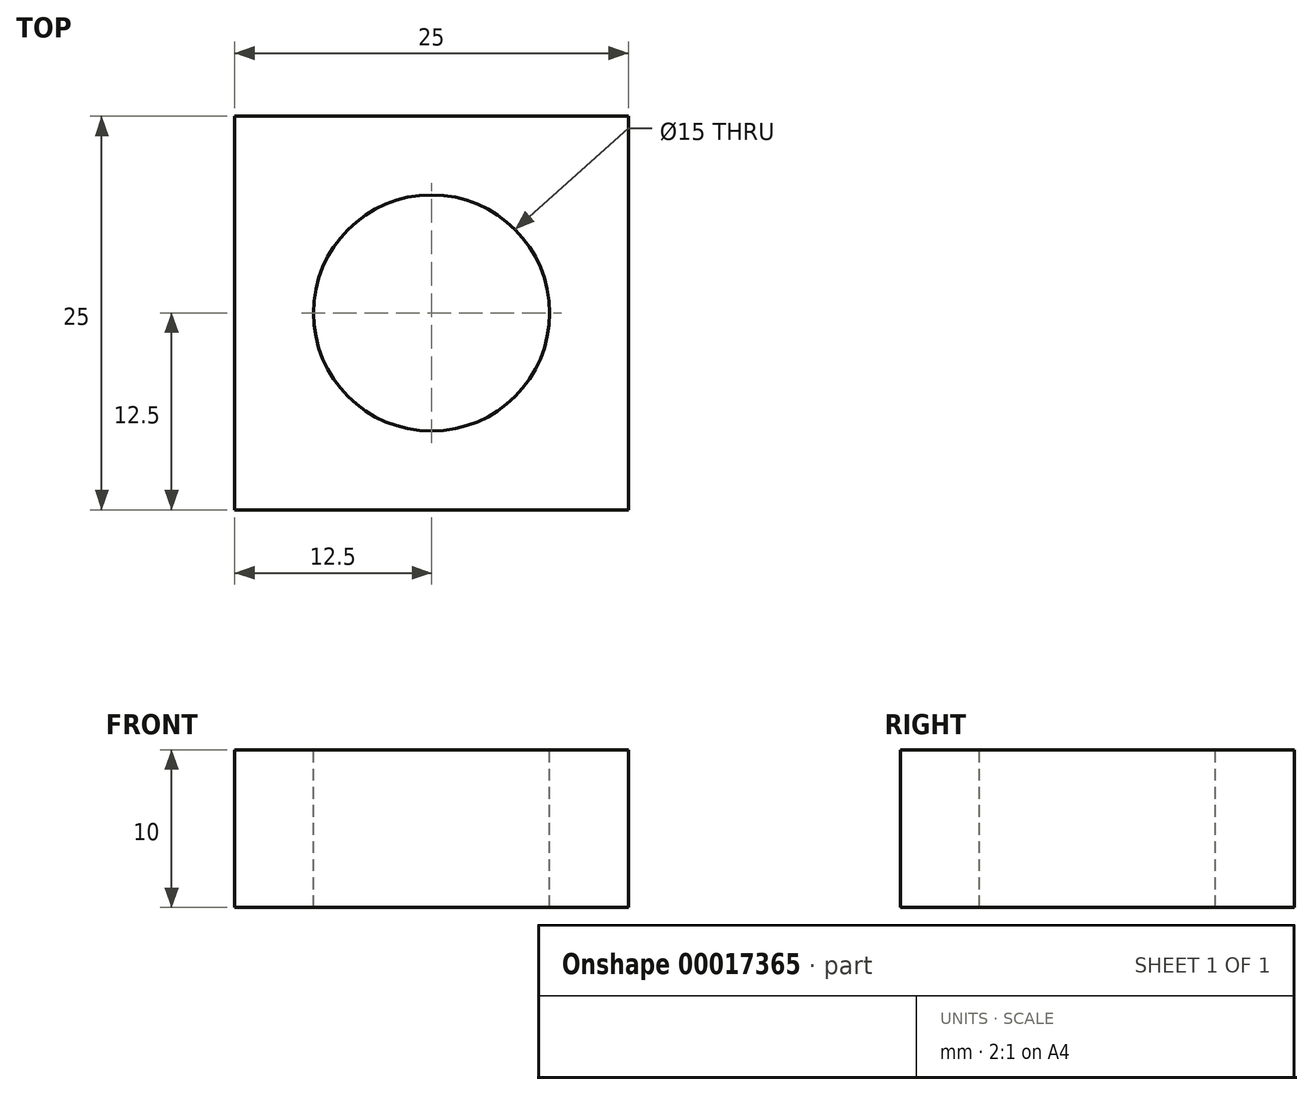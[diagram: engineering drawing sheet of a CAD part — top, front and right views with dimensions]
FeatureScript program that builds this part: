
annotation { "Feature Type Name" : "Feature", "Feature Type Description" : "" }
export const myFeature = defineFeature(function(context is Context, id is Id, definition is map)
    precondition{}
    {
        {
            var Q0;
            Q0=qCreatedBy(makeId("Front.planeOp"),FACE);
            var sketch = newSketch(context, id + "F0", { "sketchPlane" : qUnion([Q0])});
            skLineSegment(sketch, "E0", {"start": v(0, 0) * mm, "end": v(-25, 0) * mm});
            skLineSegment(sketch, "E1", {"start": v(-25, 0) * mm, "end": v(-25, 10) * mm});
            skLineSegment(sketch, "E2", {"start": v(-25, 10) * mm, "end": v(0, 10) * mm});
            skLineSegment(sketch, "E3", {"start": v(0, 10) * mm, "end": v(0, 0) * mm});
            skSolve(sketch);
        }
        {
            var Q0;
            Q0 = qSketchRegion(id + "F0", true);
            extrude(context, id + "F1", {"entities" : qUnion([Q0]), "depth" : 25 * mm});
        }
        {
            var Q0;
            Q0=makeQuery(id+"F1.opExtrude","SWEPT_FACE",FACE,{"disambiguationData":[OSD([sQuery(id+"F0.wireOp",EDGE,"E2")])]});
            var sketch = newSketch(context, id + "F2", { "sketchPlane" : qUnion([Q0])});
            skCircle(sketch, "E4", {"center": v(-12.5, -12.5) * mm, "radius": 7.5 * mm});
            skSolve(sketch);
        }
        {
            var Q0;
            Q0=makeQuery(id+"F2.imprint","IMPRINT",FACE,{"disambiguationData":[TD([[makeQuery(id+"F2.imprint","IMPRINT",EDGE,{"derivedFrom":sQuery(id+"F2.wireOp",EDGE,"E4")}),1.0]])]});
            extrude(context, id + "F3", {"entities" : qUnion([Q0]), "operationType" : NewBodyOperationType.REMOVE, "oppositeDirection" : true, "depth" : 25 * mm});
        }
    });
